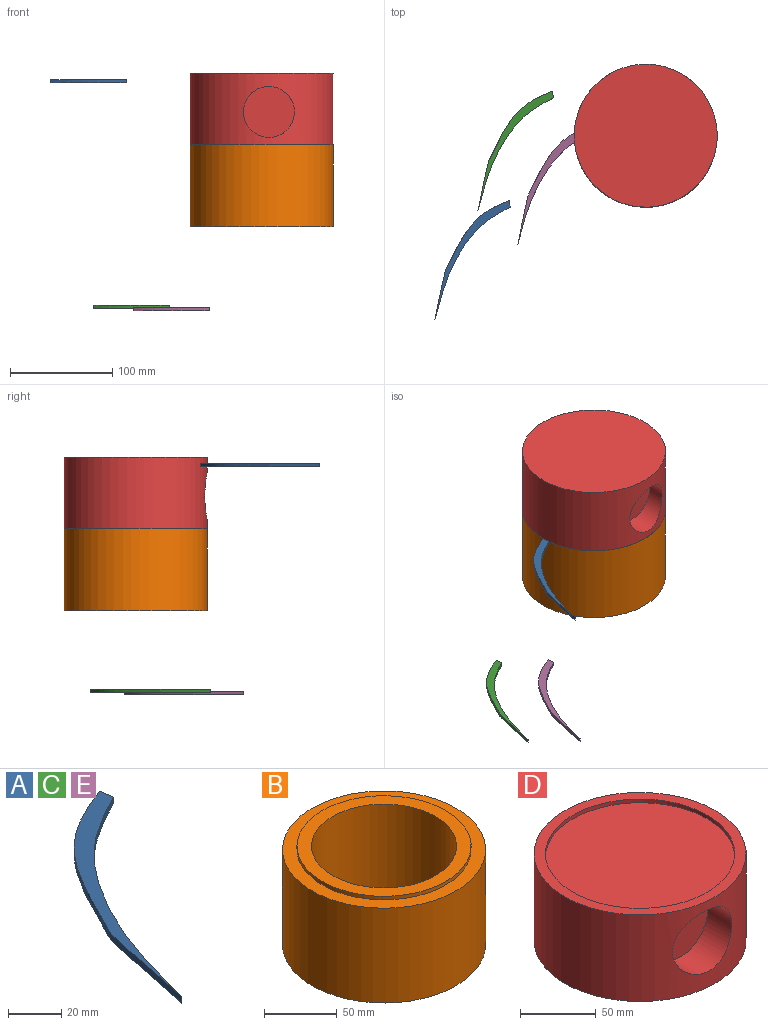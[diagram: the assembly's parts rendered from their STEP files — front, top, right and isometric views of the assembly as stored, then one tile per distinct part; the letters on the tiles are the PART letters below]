
ASSEMBLY  parts=5 mates=1
PART A: 5 faces, bbox 73.8x116.9x3 mm
  f0: plane 6.66x3mm, normal (0.99,0.14,0), area 20.2mm2, adj f1,f2,f3,f4
  f1: extruded ~116.94x72.86mm, area 436.7mm2, adj f0,f2,f3,f4
  f2: extruded ~110.28x73.82mm, area 414.1mm2, adj f0,f1,f3,f4
  f3: plane 116.94x73.82mm, normal (0,0,1), area 682.3mm2, adj f0,f1,f2
  f4: plane 116.94x73.82mm, normal (0,0,-1), area 682.3mm2, adj f0,f1,f2
PART B: 6 faces, bbox 140x140x83 mm
  f0: cylinder r=70mm len=140mm, axis (0,0,-1), area 35185.8mm2, adj f1,f2
  f1: plane 140x140mm, normal (0,0,1), area 4084.1mm2, adj f0,f4
  f2: plane 140x140mm, normal (0,0,-1), area 7539.8mm2, adj f0,f3
  f3: cylinder r=50mm len=100mm, axis (0,0,1), area 26075.2mm2, adj f2,f5
  f4: cylinder r=60mm len=120mm, axis (0,0,-1), area 1131mm2, adj f1,f5
  f5: plane 120x120mm, normal (0,0,1), area 3455.8mm2, adj f3,f4
PART C: same geometry as A
PART D: 7 faces, bbox 140x140x70 mm
  f0: cylinder r=70mm len=140mm, axis (0,0,-1), area 28780.9mm2, adj f1,f2,f3
  f1: plane 140x140mm, normal (0,0,1), area 3122mm2, adj f0,f5
  f2: plane 140x140mm, normal (0,0,-1), area 15393.8mm2, adj f0
  f3: cylinder r=25mm len=50mm, axis (0,-1,0), area 3480.4mm2, adj f0,f4
  f4: plane 50x50mm, normal (0,-1,0), area 1963.5mm2, adj f3
  f5: cylinder r=62.5mm len=125mm, axis (0,0,1), area 1178.1mm2, adj f1,f6
  f6: plane 125x125mm, normal (0,0,1), area 12271.8mm2, adj f5
PART E: same geometry as A
PLACE A t=(-47.29,56.33,280.79)mm
PLACE B t=(120.14,219.24,140.06)mm
PLACE C t=(-5.05,163.74,59.88)mm
PLACE D rot(axis=(0,-1,0),180deg) t=(32.68,194.5,290.06)mm
PLACE E t=(33.96,130.73,57.67)mm
MATE cylindrical D.f0 <-> B.f0  axis (0,0,-1) through (76.24,202.65,220.06)mm
